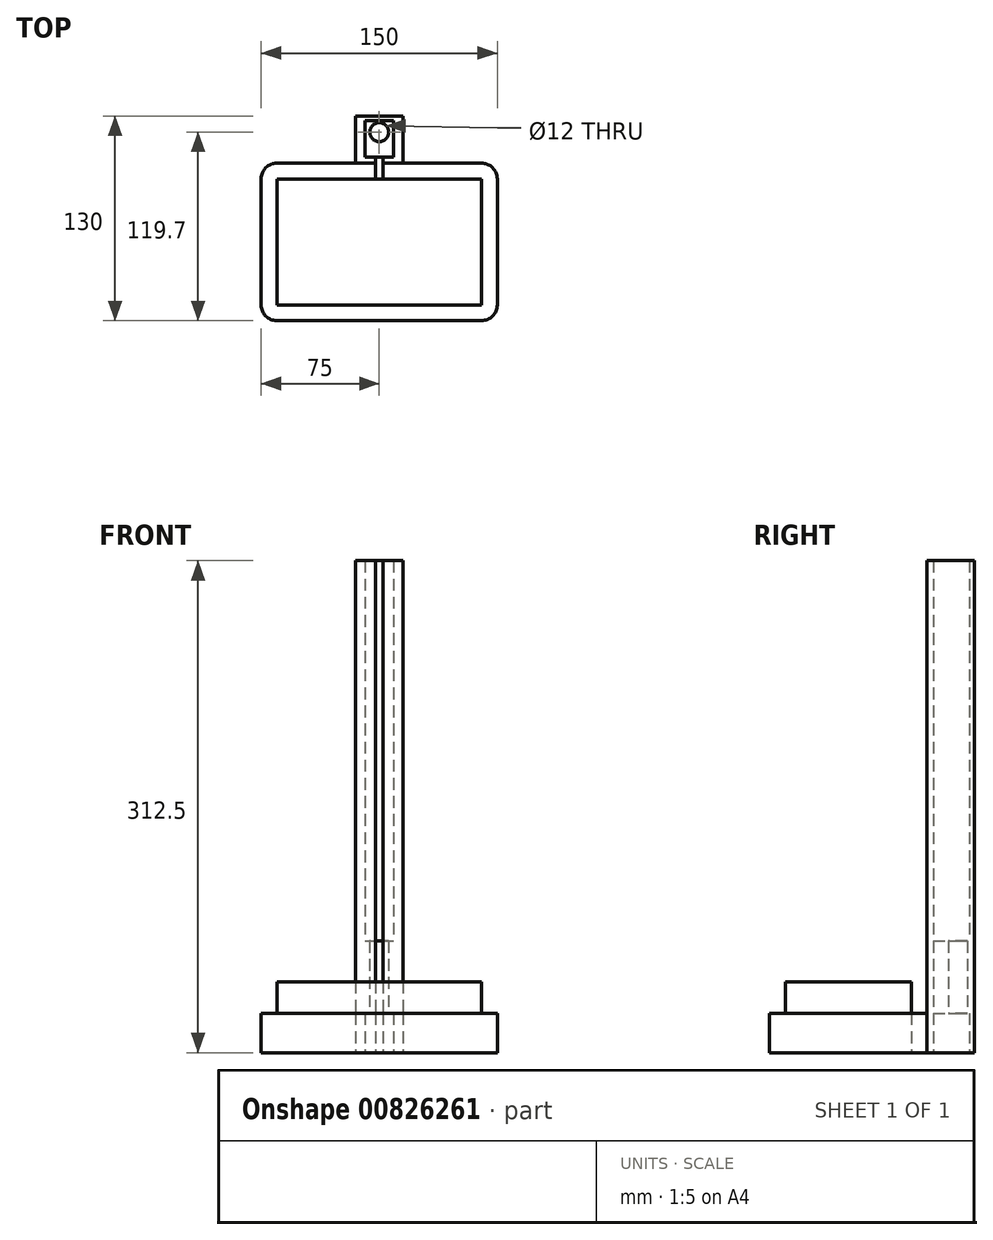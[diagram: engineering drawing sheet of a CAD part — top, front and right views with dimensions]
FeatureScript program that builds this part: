
annotation { "Feature Type Name" : "Feature", "Feature Type Description" : "" }
export const myFeature = defineFeature(function(context is Context, id is Id, definition is map)
    precondition{}
    {
        {
            var Q0;
            Q0=qCreatedBy(makeId("Top.planeOp"),FACE);
            var sketch = newSketch(context, id + "F0", { "sketchPlane" : qUnion([Q0])});
            skLineSegment(sketch, "E0.bottom", {"start": v(-65, 50) * mm, "end": v(65, 50) * mm});
            skLineSegment(sketch, "E0.top", {"start": v(-65, -50) * mm, "end": v(65, -50) * mm});
            skLineSegment(sketch, "E0.left", {"start": v(-75, 40) * mm, "end": v(-75, -40) * mm});
            skLineSegment(sketch, "E0.right", {"start": v(75, 40) * mm, "end": v(75, -40) * mm});
            skLineSegment(sketch, "E1", {"start": v(0, 0) * mm, "end": v(-75, 0) * mm, "construction": true});
            skLineSegment(sketch, "E2", {"start": v(0, 0) * mm, "end": v(0, -50) * mm, "construction": true});
            skLineSegment(sketch, "E3.bottom", {"start": v(-15, 80) * mm, "end": v(15, 80) * mm});
            skLineSegment(sketch, "E3.top", {"start": v(-15, 50) * mm, "end": v(15, 50) * mm});
            skLineSegment(sketch, "E3.left", {"start": v(-15, 80) * mm, "end": v(-15, 50) * mm});
            skLineSegment(sketch, "E3.right", {"start": v(15, 80) * mm, "end": v(15, 50) * mm});
            skLineSegment(sketch, "E4", {"start": v(0, 0) * mm, "end": v(0, 80) * mm, "construction": true});
            skLineSegment(sketch, "E5.bottom", {"start": v(-65, 40) * mm, "end": v(65, 40) * mm});
            skLineSegment(sketch, "E5.top", {"start": v(-65, -40) * mm, "end": v(65, -40) * mm});
            skLineSegment(sketch, "E5.left", {"start": v(-65, 40) * mm, "end": v(-65, -40) * mm});
            skLineSegment(sketch, "E5.right", {"start": v(65, 40) * mm, "end": v(65, -40) * mm});
            skLineSegment(sketch, "E6.bottom", {"start": v(-2.5, 59.58) * mm, "end": v(2.5, 59.58) * mm});
            skLineSegment(sketch, "E6.top", {"start": v(-2.5, 40) * mm, "end": v(2.5, 40) * mm});
            skLineSegment(sketch, "E6.left", {"start": v(-2.5, 59.58) * mm, "end": v(-2.5, 40) * mm});
            skLineSegment(sketch, "E6.right", {"start": v(2.5, 59.58) * mm, "end": v(2.5, 40) * mm});
            skLineSegment(sketch, "E7", {"start": v(0, 0) * mm, "end": v(-65, 0) * mm, "construction": true});
            skPoint(sketch, "E8.visualSharp", {"position": v(-75, 50) * mm});
            skArc(sketch, "E8.filletArc", {"start": v(-65, 50) * mm, "mid": v(-72.07, 47.07) * mm, "end": v(-75, 40) * mm});
            skPoint(sketch, "E9.visualSharp", {"position": v(75, 50) * mm});
            skArc(sketch, "E9.filletArc", {"start": v(75, 40) * mm, "mid": v(72.07, 47.07) * mm, "end": v(65, 50) * mm});
            skPoint(sketch, "E10.visualSharp", {"position": v(-75, -50) * mm});
            skArc(sketch, "E10.filletArc", {"start": v(-75, -40) * mm, "mid": v(-72.07, -47.07) * mm, "end": v(-65, -50) * mm});
            skPoint(sketch, "E11.visualSharp", {"position": v(75, -50) * mm});
            skArc(sketch, "E11.filletArc", {"start": v(65, -50) * mm, "mid": v(72.07, -47.07) * mm, "end": v(75, -40) * mm});
            skLineSegment(sketch, "E12", {"start": v(0, 0) * mm, "end": v(0, 40) * mm});
            skCircle(sketch, "E13", {"center": v(0, 69.7) * mm, "radius": 6 * mm});
            skLineSegment(sketch, "E14", {"start": v(-9, 54) * mm, "end": v(-9, 77) * mm});
            skLineSegment(sketch, "E15", {"start": v(-9, 77) * mm, "end": v(9, 77) * mm});
            skLineSegment(sketch, "E16", {"start": v(0, 79.25) * mm, "end": v(0, 80) * mm});
            skLineSegment(sketch, "E17", {"start": v(-9, 54) * mm, "end": v(9, 54) * mm});
            skLineSegment(sketch, "E18", {"start": v(9, 54) * mm, "end": v(9, 77) * mm});
            skLineSegment(sketch, "E19", {"start": v(0, 77) * mm, "end": v(0, 80) * mm});
            skSolve(sketch);
        }
        {
            var Q0;
            Q0=makeQuery(id+"F0.imprint","IMPRINT",FACE,{"disambiguationData":[TD([[makeQuery(id+"F0.imprint","IMPRINT",EDGE,{"derivedFrom":sQuery(id+"F0.wireOp",EDGE,"E0.top")}),1.0]])]});
            var Q1;
            {var subQ5=sQuery(id+"F0.wireOp",EDGE,"E6.top");Q1=makeQuery(id+"F0.imprint","IMPRINT",FACE,{"disambiguationData":[TD([[makeQuery(id+"F0.imprint","IMPRINT",EDGE,{"derivedFrom":subQ5}),1.0]])]});}
            var Q2;
            {var subQ0=sQuery(id+"F0.wireOp",EDGE,"l1MtYh9c-CzXV-YJr5-94RZ-eUTwZ6HwwpDR");Q2=makeQuery(id+"F0.imprint","IMPRINT",FACE,{"disambiguationData":[TD([[makeQuery(id+"F0.imprint","IMPRINT",EDGE,{"derivedFrom":subQ0}),1.0]])]});}
            extrude(context, id + "F1", {"entities" : qUnion([Q0, Q1, Q2]), "endBound" : BoundingType.SYMMETRIC, "depth" : 25 * mm, "offsetDistance" : 25 * mm});
        }
        {
            var Q0;
            Q0=makeQuery(id+"F0.imprint","IMPRINT",FACE,{"disambiguationData":[TD([[makeQuery(id+"F0.imprint","IMPRINT",EDGE,{"derivedFrom":sQuery(id+"F0.wireOp",EDGE,"E3.bottom")}),-1.0]])]});
            var Q1;
            {var subQ0=sQuery(id+"F0.wireOp",EDGE,"iEGK5Bb7-SoDk-IzIK-Jkqt-TQqyKEJhDGZO");Q1=makeQuery(id+"F0.imprint","IMPRINT",FACE,{"disambiguationData":[TD([[makeQuery(id+"F0.imprint","IMPRINT",EDGE,{"derivedFrom":subQ0}),1.0]])]});}
            extrude(context, id + "F2", {"entities" : qUnion([Q0, Q1]), "operationType" : NewBodyOperationType.ADD, "depth" : 300 * mm, "offsetDistance" : 25 * mm, "hasSecondDirection" : true, "secondDirectionOppositeDirection" : true, "secondDirectionDepth" : 12.5 * mm});
        }
        {
            var Q0;
            Q0=makeQuery(id+"F1.opExtrude","CAP_FACE",FACE,{"disambiguationData":[OSD([sQuery(id+"F0.wireOp",EDGE,"E0.bottom"),sQuery(id+"F0.wireOp",EDGE,"E0.top"),sQuery(id+"F0.wireOp",EDGE,"E0.left"),sQuery(id+"F0.wireOp",EDGE,"E0.right"),sQuery(id+"F0.wireOp",EDGE,"E3.top"),sQuery(id+"F0.wireOp",EDGE,"E5.bottom"),sQuery(id+"F0.wireOp",EDGE,"E5.top"),sQuery(id+"F0.wireOp",EDGE,"E5.left"),sQuery(id+"F0.wireOp",EDGE,"E5.right"),sQuery(id+"F0.wireOp",EDGE,"E6.top"),sQuery(id+"F0.wireOp",EDGE,"E8.filletArc"),sQuery(id+"F0.wireOp",EDGE,"E9.filletArc"),sQuery(id+"F0.wireOp",EDGE,"E10.filletArc"),sQuery(id+"F0.wireOp",EDGE,"E11.filletArc")])],"isStart":false});
            var sketch = newSketch(context, id + "F3", { "sketchPlane" : qUnion([Q0])});
            skLineSegment(sketch, "E20.0", {"start": v(-65, 40) * mm, "end": v(-65, -40) * mm});
            skLineSegment(sketch, "E20.1", {"start": v(-65, 40) * mm, "end": v(65, 40) * mm});
            skLineSegment(sketch, "E20.2", {"start": v(65, 40) * mm, "end": v(65, -40) * mm});
            skLineSegment(sketch, "E20.3", {"start": v(-65, -40) * mm, "end": v(65, -40) * mm});
            skLineSegment(sketch, "E21.0", {"start": v(-2.5, 59.58) * mm, "end": v(-2.5, 40) * mm});
            skLineSegment(sketch, "E21.1", {"start": v(2.5, 59.58) * mm, "end": v(2.5, 40) * mm});
            skSolve(sketch);
        }
        {
            var Q0;
            {var subQ0=sQuery(id+"F3.wireOp",EDGE,"E21.0");var subQ1=sQuery(id+"F3.wireOp",EDGE,"E20.1");var subQ2=makeQuery(id+"F3.imprint","INTERSECT",VERTEX,{"derivedFrom":[subQ1,subQ0]});Q0=makeQuery(id+"F3.imprint","IMPRINT",FACE,{"disambiguationData":[TD([[makeQuery(id+"F3.imprint","IMPRINT",EDGE,{"disambiguationData":[TD([[subQ2,-1.0]])],"derivedFrom":subQ1}),1.0]])]});}
            var Q1;
            Q1=makeQuery(id+"F3.imprint","IMPRINT",FACE,{"disambiguationData":[TD([[makeQuery(id+"F3.imprint","IMPRINT",EDGE,{"derivedFrom":sQuery(id+"F3.wireOp",EDGE,"E21.2")}),1.0]])]});
            var Q2;
            {var subQ4=sQuery(id+"F3.wireOp",EDGE,"E20.0");Q2=makeQuery(id+"F3.imprint","IMPRINT",FACE,{"disambiguationData":[TD([[makeQuery(id+"F3.imprint","IMPRINT",EDGE,{"derivedFrom":subQ4}),1.0]])]});}
            extrude(context, id + "F4", {"entities" : qUnion([Q0, Q1, Q2]), "depth" : 20 * mm, "offsetDistance" : 25 * mm});
        }
        {
            var Q0;
            {var subQ4=sQuery(id+"F3.wireOp",EDGE,"E20.0");Q0=makeQuery(id+"F3.imprint","IMPRINT",FACE,{"disambiguationData":[TD([[makeQuery(id+"F3.imprint","IMPRINT",EDGE,{"derivedFrom":subQ4}),1.0]])]});}
            extrude(context, id + "F5", {"entities" : qUnion([Q0]), "operationType" : NewBodyOperationType.ADD, "oppositeDirection" : true, "depth" : 25 * mm, "offsetDistance" : 25 * mm});
        }
        {
            var Q0;
            Q0=makeQuery(id+"F0.imprint","IMPRINT",FACE,{"disambiguationData":[TD([[makeQuery(id+"F0.imprint","IMPRINT",EDGE,{"derivedFrom":sQuery(id+"F0.wireOp",EDGE,"E13")}),1.0]])]});
            extrude(context, id + "F6", {"entities" : qUnion([Q0]), "operationType" : NewBodyOperationType.REMOVE, "depth" : 50 * mm, "offsetDistance" : 25 * mm});
        }
        {
            var Q0;
            {var subQ0=sQuery(id+"F0.wireOp",EDGE,"E6.bottom");Q0=makeQuery(id+"F0.imprint","IMPRINT",FACE,{"disambiguationData":[TD([[makeQuery(id+"F0.imprint","IMPRINT",EDGE,{"derivedFrom":subQ0}),-1.0]])]});}
            var Q1;
            {var subQ1=sQuery(id+"F0.wireOp",EDGE,"E6.bottom");Q1=makeQuery(id+"F0.imprint","IMPRINT",FACE,{"disambiguationData":[TD([[makeQuery(id+"F0.imprint","IMPRINT",EDGE,{"derivedFrom":subQ1}),1.0]])]});}
            var Q2;
            {var subQ0=sQuery(id+"F0.wireOp",EDGE,"E6.left");var subQ1=sQuery(id+"F0.wireOp",EDGE,"E3.top");var subQ2=makeQuery(id+"F0.imprint","INTERSECT",VERTEX,{"derivedFrom":[subQ1,subQ0]});Q2=makeQuery(id+"F0.imprint","IMPRINT",FACE,{"disambiguationData":[TD([[makeQuery(id+"F0.imprint","IMPRINT",EDGE,{"disambiguationData":[TD([[subQ2,-1.0]])],"derivedFrom":subQ1}),1.0]])]});}
            extrude(context, id + "F7", {"entities" : qUnion([Q0, Q1, Q2]), "operationType" : NewBodyOperationType.ADD, "depth" : 58.5 * mm, "offsetDistance" : 25 * mm});
        }
        {
            var Q0;
            {var subQ0=sQuery(id+"F0.wireOp",EDGE,"E6.left");var subQ1=sQuery(id+"F0.wireOp",EDGE,"E3.top");var subQ2=makeQuery(id+"F0.imprint","INTERSECT",VERTEX,{"derivedFrom":[subQ1,subQ0]});Q0=makeQuery(id+"F0.imprint","IMPRINT",FACE,{"disambiguationData":[TD([[makeQuery(id+"F0.imprint","IMPRINT",EDGE,{"disambiguationData":[TD([[subQ2,-1.0]])],"derivedFrom":subQ1}),1.0]])]});}
            var Q1;
            {var subQ0=sQuery(id+"F0.wireOp",EDGE,"E6.bottom");Q1=makeQuery(id+"F0.imprint","IMPRINT",FACE,{"disambiguationData":[TD([[makeQuery(id+"F0.imprint","IMPRINT",EDGE,{"derivedFrom":subQ0}),-1.0]])]});}
            var Q2;
            {var subQ1=sQuery(id+"F0.wireOp",EDGE,"E6.bottom");Q2=makeQuery(id+"F0.imprint","IMPRINT",FACE,{"disambiguationData":[TD([[makeQuery(id+"F0.imprint","IMPRINT",EDGE,{"derivedFrom":subQ1}),1.0]])]});}
            extrude(context, id + "F8", {"entities" : qUnion([Q0, Q1, Q2]), "operationType" : NewBodyOperationType.REMOVE, "depth" : 12.5 * mm, "offsetDistance" : 25 * mm});
        }
    });
